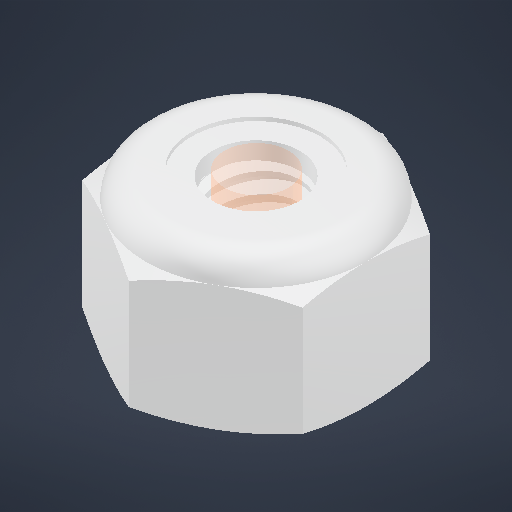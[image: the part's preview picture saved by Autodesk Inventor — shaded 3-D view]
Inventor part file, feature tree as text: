
AUTODESK INVENTOR PART (.ipt)
format: ipt  version: 2025.2 (Build 292293000, 293)  size: 373,248 bytes
history: native  units: in
note: dims shown in document units (in); Inventor stores cm internally (conversion verified against a paired STEP export)
features: other x2, sketch x1, revolve x1, extrude x1
ambient origin geometry x8: Origin, YZ Plane, XZ Plane, XY Plane, X Axis, Y Axis, Z Axis, Center Point
bodies: Solid1 (feature_tree), Solid2 (feature_tree)
feature tree (5):
  sketch  "Sketch1"  dims[d1=0.1in d2=0.234in d3=0.0in]
  other  "Srf1"
  other  "Cut-Revolve4"
  revolve  "Revolve2"  [1 undecoded]
  extrude  "ExtrusionSrf1"  [1 undecoded]
note: 2 required parameter values undecoded (feature->parameter linkage not recoverable at this tier; creation-order binding heuristic only, values carry confidence <= 0.55)